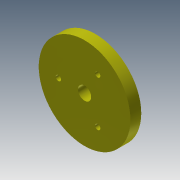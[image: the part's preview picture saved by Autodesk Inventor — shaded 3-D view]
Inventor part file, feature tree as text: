
AUTODESK INVENTOR PART (.ipt)
format: ipt  version: 2013 (Build 170138000, 138)  size: 124,928 bytes
history: native  units: mm
features: sketch x7, extrude x6
ambient origin geometry x8: Origin, YZ Plane, XZ Plane, XY Plane, X Axis, Y Axis, Z Axis, Center Point
bodies: Solid1 (feature_tree)
feature tree (13):
  extrude  "Extrusion1"  Depth=5.0mm
  extrude  "Extrusion2"  Depth=3.0mm
  extrude  "Extrusion3"  Depth=3.0mm
  extrude  "Extrusion4"  Depth=34.65mm
  extrude  "Extrusion5"  Depth=3.8mm TaperAngle=0.0deg
  sketch  "Sketch6"  dims[d16=2.0mm d19=2.0mm]
  extrude  "Extrusion6"  Depth=2.0mm
  sketch  "Sketch1"  dims[d0=33.15mm d1=5.0mm]
  sketch  "Sketch2"  dims[d2=3.8mm d3=0.0mm d4=3.0mm]
  sketch  "Sketch3"  dims[d7=3.0mm d8=3.0mm]
  sketch  "Sketch4"  dims[d9=3.8mm d10=0.0mm d11=34.65mm]
  sketch  "Sketch5"  dims[d12=3.8mm d13=0.0mm d14=3.8mm d15=0.0mm]
  sketch  "Sketch7"  dims[d20=2.0mm d21=3.8mm d22=0.0mm d23=0.3mm d24=0.0mm]
